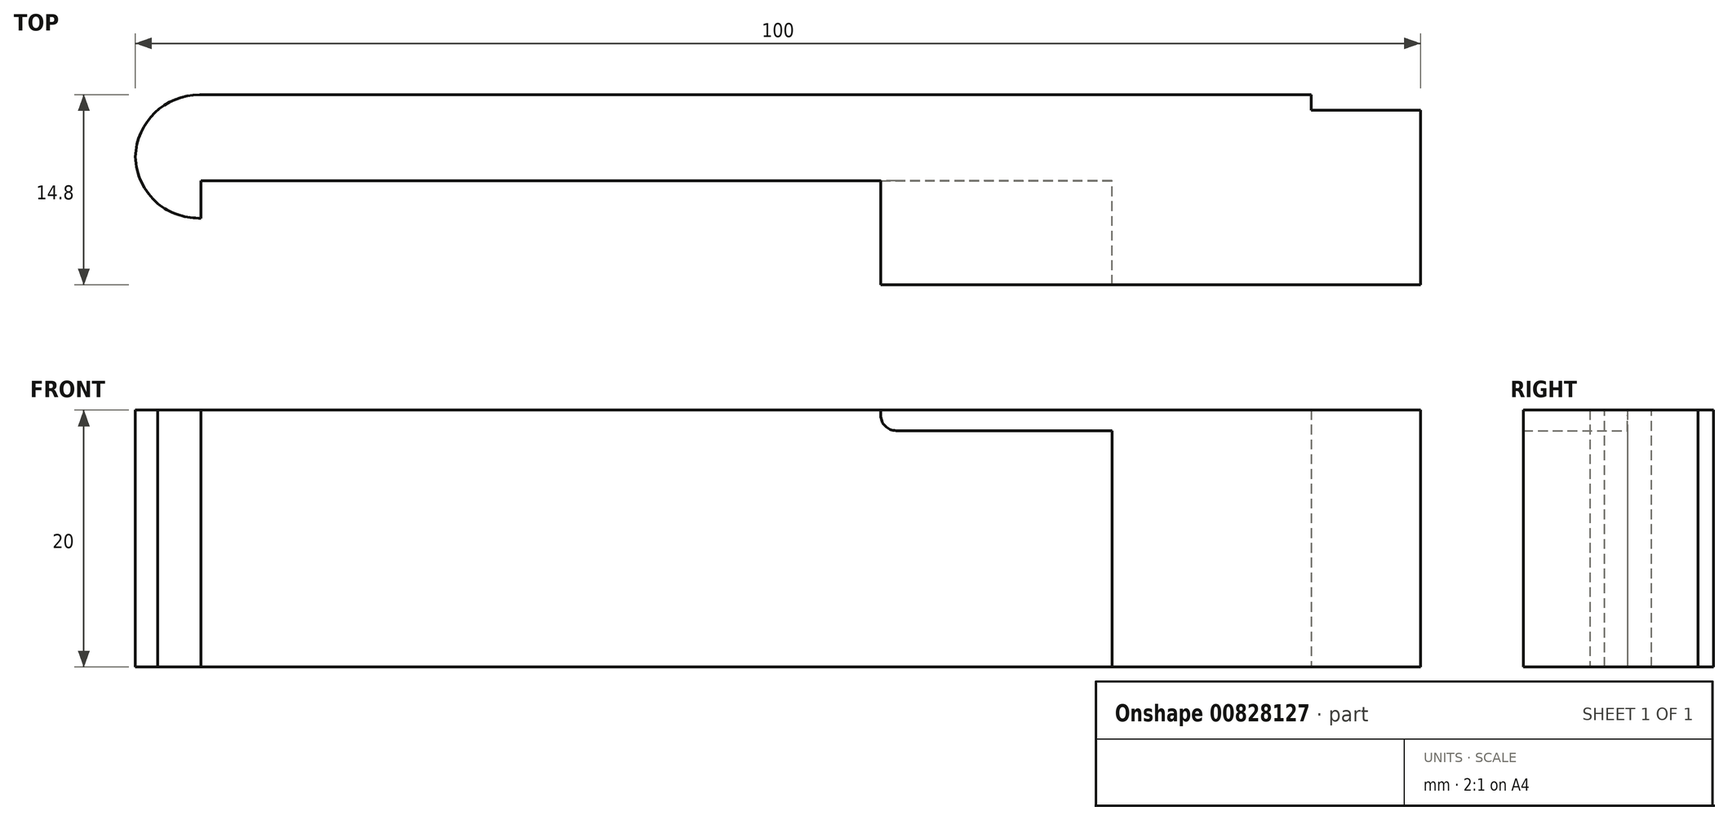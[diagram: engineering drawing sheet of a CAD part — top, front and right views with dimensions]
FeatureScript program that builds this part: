
annotation { "Feature Type Name" : "Feature", "Feature Type Description" : "" }
export const myFeature = defineFeature(function(context is Context, id is Id, definition is map)
    precondition{}
    {
        {
            var Q0;
            Q0=qCreatedBy(makeId("Top.planeOp"),FACE);
            var sketch = newSketch(context, id + "F0", { "sketchPlane" : qUnion([Q0])});
            skLineSegment(sketch, "E0.bottom", {"start": v(-8.5, 0.2) * mm, "end": v(-24, 0.2) * mm});
            skLineSegment(sketch, "E0.top", {"start": v(-8.5, 15) * mm, "end": v(-100, 15) * mm});
            skLineSegment(sketch, "E0.left", {"start": v(0, 1.7) * mm, "end": v(0, 13.8) * mm});
            skLineSegment(sketch, "E0.right", {"start": v(-100, 8) * mm, "end": v(-100, 15) * mm});
            skLineSegment(sketch, "E1", {"start": v(-24, 0.2) * mm, "end": v(-24, 8.3) * mm});
            skLineSegment(sketch, "E2", {"start": v(-94.9, 8.3) * mm, "end": v(-94.9, 5.4) * mm});
            skLineSegment(sketch, "E3", {"start": v(-94.9, 5.4) * mm, "end": v(-96.9, 5.4) * mm});
            skLineSegment(sketch, "E4.trimOffspring", {"start": v(-94.9, 8.3) * mm, "end": v(-24, 8.3) * mm});
            skLineSegment(sketch, "E5", {"start": v(-100, 8) * mm, "end": v(-96.9, 5.4) * mm});
            skLineSegment(sketch, "E6", {"start": v(0, 1.7) * mm, "end": v(0, 0.2) * mm});
            skLineSegment(sketch, "E7", {"start": v(0, 0.2) * mm, "end": v(-8.5, 0.2) * mm});
            skLineSegment(sketch, "E8", {"start": v(-8.5, 15) * mm, "end": v(-8.5, 13.8) * mm});
            skLineSegment(sketch, "E9", {"start": v(-8.5, 13.8) * mm, "end": v(0, 13.8) * mm});
            skSolve(sketch);
        }
        {
            var Q0;
            Q0=makeQuery(id+"F0.imprint","IMPRINT",FACE,{"disambiguationData":[TD([[makeQuery(id+"F0.imprint","IMPRINT",EDGE,{"derivedFrom":sQuery(id+"F0.wireOp",EDGE,"E0.bottom")}),-1.0]])]});
            extrude(context, id + "F1", {"entities" : qUnion([Q0]), "depth" : 20 * mm, "offsetDistance" : 25 * mm});
        }
        {
            var Q0;
            Q0=makeQuery(id+"F1.opExtrude","SWEPT_FACE",FACE,{"disambiguationData":[OSD([sQuery(id+"F0.wireOp",EDGE,"E4.trimOffspring")])]});
            var sketch = newSketch(context, id + "F2", { "sketchPlane" : qUnion([Q0])});
            skLineSegment(sketch, "E10.bottom", {"start": v(-24, 20) * mm, "end": v(-42, 20) * mm});
            skLineSegment(sketch, "E10.top", {"start": v(-24, 18.4) * mm, "end": v(-42, 18.4) * mm});
            skLineSegment(sketch, "E10.left", {"start": v(-24, 20) * mm, "end": v(-24, 18.4) * mm});
            skLineSegment(sketch, "E10.right", {"start": v(-42, 20) * mm, "end": v(-42, 18.4) * mm});
            skSolve(sketch);
        }
        {
            var Q0;
            Q0=makeQuery(id+"F2.imprint","IMPRINT",FACE,{"disambiguationData":[TD([[makeQuery(id+"F2.imprint","IMPRINT",EDGE,{"derivedFrom":sQuery(id+"F2.wireOp",EDGE,"E10.bottom")}),-1.0]])]});
            extrude(context, id + "F3", {"entities" : qUnion([Q0]), "operationType" : NewBodyOperationType.ADD, "depth" : 8.1 * mm, "offsetDistance" : 25 * mm});
        }
        {
            var Q0;
            Q0=makeQuery(id+"F3.opExtrude","SWEPT_EDGE",EDGE,{"disambiguationData":[OSD([sQuery(id+"F2.wireOp",EDGE,"E10.top"),sQuery(id+"F2.wireOp",EDGE,"E10.right")])]});
            fillet(context, id + "F4", {"entities" : qUnion([Q0]), "radius" : 1.2 * mm, "tangentPropagation" : true, "allowEdgeOverflow" : false});
        }
        {
            var Q0;
            Q0=makeQuery(id+"F1.opExtrude","SWEPT_EDGE",EDGE,{"disambiguationData":[OSD([sQuery(id+"F0.wireOp",EDGE,"E3"),sQuery(id+"F0.wireOp",EDGE,"E5")])]});
            var Q1;
            Q1=makeQuery(id+"F1.opExtrude","SWEPT_EDGE",EDGE,{"disambiguationData":[OSD([sQuery(id+"F0.wireOp",EDGE,"E0.right"),sQuery(id+"F0.wireOp",EDGE,"E5")])]});
            var Q2;
            Q2=makeQuery(id+"F1.opExtrude","SWEPT_EDGE",EDGE,{"disambiguationData":[OSD([sQuery(id+"F0.wireOp",EDGE,"E0.top"),sQuery(id+"F0.wireOp",EDGE,"E0.right")])]});
            fillet(context, id + "F5", {"entities" : qUnion([Q0, Q1, Q2]), "radius" : 5 * mm, "tangentPropagation" : true, "allowEdgeOverflow" : false});
        }
    });
